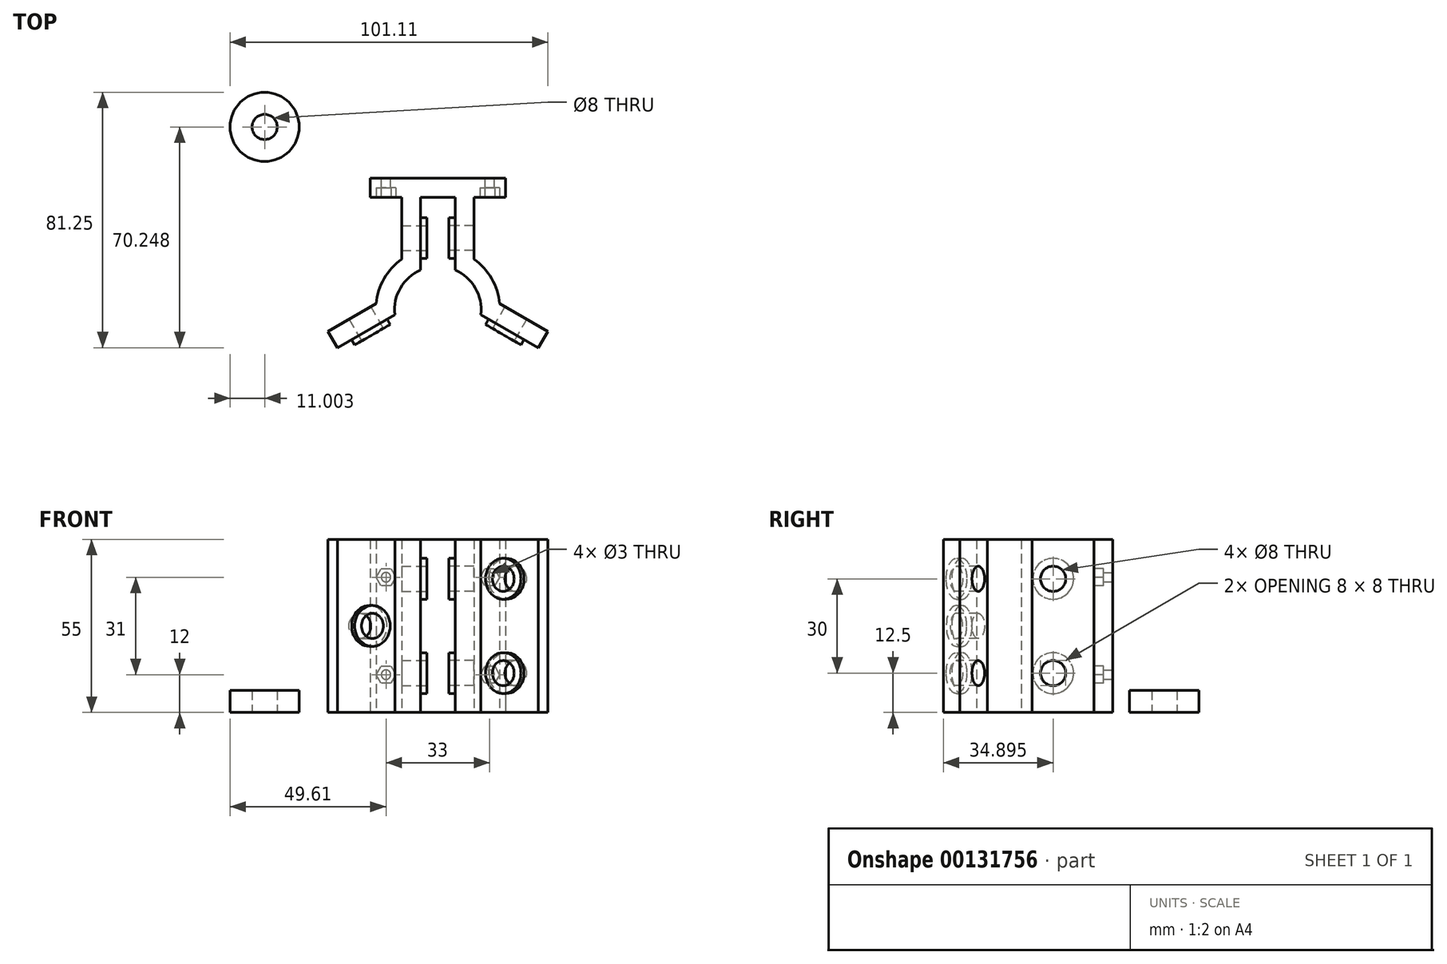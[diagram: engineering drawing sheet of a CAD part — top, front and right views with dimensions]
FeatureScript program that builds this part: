
annotation { "Feature Type Name" : "Feature", "Feature Type Description" : "" }
export const myFeature = defineFeature(function(context is Context, id is Id, definition is map)
    precondition{}
    {
        {
            assignVariable(context, id + "F0", {"name" : "bgap", "anyValue" : 2});
        }
        {
            assignVariable(context, id + "F1", {"name" : "bhole", "anyValue" : 8});
        }
        {
            assignVariable(context, id + "F2", {"name" : "bwidth", "anyValue" : 7});
        }
        {
            assignVariable(context, id + "F3", {"name" : "bdiam", "anyValue" : 22});
        }
        {
            assignVariable(context, id + "F4", {"name" : "width", "anyValue" : 6});
        }
        {
            assignVariable(context, id + "F5", {"name" : "blockLength", "anyValue" : getVariable(context, 'bdiam') * 2 + getVariable(context, 'bdiam') / 2});
        }
        {
            assignVariable(context, id + "F6", {"name" : "mBoltDiam", "anyValue" : 3});
        }
        {
            var Q0;
            Q0=qCreatedBy(makeId("Top.planeOp"),FACE);
            var sketch = newSketch(context, id + "F7", { "sketchPlane" : qUnion([Q0])});
            skCircle(sketch, "E0", {"center": v(0, 0) * mm, "radius": 11.78 * mm, "construction": true});
            skLineSegment(sketch, "E1", {"start": v(0, 0) * mm, "end": v(0, 20) * mm, "construction": true});
            skLineSegment(sketch, "E2", {"start": v(0, 0) * mm, "end": v(-17.32, -10) * mm, "construction": true});
            skLineSegment(sketch, "E3", {"start": v(0, 0) * mm, "end": v(17.32, -10) * mm, "construction": true});
            skPoint(sketch, "E4", {"position": v(0, 22.77) * mm});
            skPoint(sketch, "E5", {"position": v(19.72, -11.39) * mm});
            skPoint(sketch, "E6", {"position": v(-19.72, -11.39) * mm});
            skLineSegment(sketch, "E7.bottom", {"start": v(-3.5, 33.77) * mm, "end": v(3.5, 33.77) * mm, "construction": true});
            skLineSegment(sketch, "E7.top", {"start": v(-3.5, 11.78) * mm, "end": v(3.5, 11.78) * mm, "construction": true});
            skLineSegment(sketch, "E7.left", {"start": v(-3.5, 33.77) * mm, "end": v(-3.5, 11.78) * mm, "construction": true});
            skLineSegment(sketch, "E7.right", {"start": v(3.5, 33.77) * mm, "end": v(3.5, 11.78) * mm, "construction": true});
            skLineSegment(sketch, "E8", {"start": v(-31, -13.86) * mm, "end": v(-27.5, -19.92) * mm, "construction": true});
            skLineSegment(sketch, "E9", {"start": v(-27.5, -19.92) * mm, "end": v(-8.45, -8.92) * mm, "construction": true});
            skLineSegment(sketch, "E10", {"start": v(-8.45, -8.92) * mm, "end": v(-11.95, -2.86) * mm, "construction": true});
            skLineSegment(sketch, "E11", {"start": v(-11.95, -2.86) * mm, "end": v(-31, -13.86) * mm, "construction": true});
            skLineSegment(sketch, "E12", {"start": v(31, -13.86) * mm, "end": v(27.5, -19.92) * mm, "construction": true});
            skLineSegment(sketch, "E13", {"start": v(27.5, -19.92) * mm, "end": v(8.45, -8.92) * mm, "construction": true});
            skLineSegment(sketch, "E14", {"start": v(8.45, -8.92) * mm, "end": v(11.95, -2.86) * mm, "construction": true});
            skLineSegment(sketch, "E15", {"start": v(11.95, -2.86) * mm, "end": v(31, -13.86) * mm, "construction": true});
            skLineSegment(sketch, "E16", {"start": v(-31, -13.86) * mm, "end": v(-36, -5.2) * mm, "construction": true});
            skLineSegment(sketch, "E17", {"start": v(-27.5, -19.92) * mm, "end": v(-22.5, -28.58) * mm, "construction": true});
            skLineSegment(sketch, "E18", {"start": v(27.5, -19.92) * mm, "end": v(22.5, -28.58) * mm, "construction": true});
            skLineSegment(sketch, "E19", {"start": v(31, -13.86) * mm, "end": v(36, -5.2) * mm, "construction": true});
            skSolve(sketch);
        }
        {
            var Q0;
            Q0=qCreatedBy(makeId("Top.planeOp"),FACE);
            var sketch = newSketch(context, id + "F8", { "sketchPlane" : qUnion([Q0])});
            skLineSegment(sketch, "E20", {"start": v(-5.5, 12.63) * mm, "end": v(-5.5, 35.78) * mm});
            skLineSegment(sketch, "E21", {"start": v(-5.5, 35.77) * mm, "end": v(5.5, 35.77) * mm});
            skLineSegment(sketch, "E22", {"start": v(5.5, 35.77) * mm, "end": v(5.5, 12.63) * mm});
            skLineSegment(sketch, "E23", {"start": v(-11.5, 16.09) * mm, "end": v(-11.5, 41.77) * mm});
            skLineSegment(sketch, "E24", {"start": v(-11.5, 41.77) * mm, "end": v(11.5, 41.77) * mm});
            skLineSegment(sketch, "E25", {"start": v(11.5, 41.77) * mm, "end": v(11.5, 16.09) * mm});
            skArc(sketch, "E26", {"start": v(13.69, -1.55) * mm, "mid": v(11.93, 6.89) * mm, "end": v(5.5, 12.63) * mm});
            skArc(sketch, "E27", {"start": v(-13.69, -1.55) * mm, "mid": v(-11.93, 6.89) * mm, "end": v(-5.5, 12.63) * mm});
            skLineSegment(sketch, "E28", {"start": v(-32, -12.12) * mm, "end": v(-35, -6.93) * mm});
            skLineSegment(sketch, "E29", {"start": v(-35, -6.93) * mm, "end": v(-19.68, 1.92) * mm});
            skArc(sketch, "E30", {"start": v(-19.68, 1.92) * mm, "mid": v(-17.13, 9.89) * mm, "end": v(-11.5, 16.09) * mm});
            skLineSegment(sketch, "E31", {"start": v(32, -12.12) * mm, "end": v(35, -6.93) * mm});
            skLineSegment(sketch, "E32", {"start": v(35, -6.93) * mm, "end": v(19.68, 1.92) * mm});
            skArc(sketch, "E33", {"start": v(11.5, 16.09) * mm, "mid": v(17.13, 9.89) * mm, "end": v(19.68, 1.92) * mm});
            skLineSegment(sketch, "E34", {"start": v(-13.69, -1.55) * mm, "end": v(-32, -12.12) * mm});
            skLineSegment(sketch, "E35", {"start": v(13.69, -1.55) * mm, "end": v(32, -12.12) * mm});
            skLineSegment(sketch, "E36", {"start": v(-11.5, 35.78) * mm, "end": v(-21.5, 35.78) * mm});
            skLineSegment(sketch, "E37", {"start": v(-21.5, 35.78) * mm, "end": v(-21.5, 41.77) * mm});
            skLineSegment(sketch, "E38", {"start": v(-21.5, 41.77) * mm, "end": v(-11.5, 41.77) * mm});
            skLineSegment(sketch, "E39", {"start": v(11.5, 35.77) * mm, "end": v(21.5, 35.77) * mm});
            skLineSegment(sketch, "E40", {"start": v(21.5, 35.77) * mm, "end": v(21.5, 41.77) * mm});
            skLineSegment(sketch, "E41", {"start": v(21.5, 41.77) * mm, "end": v(11.5, 41.77) * mm});
            skSolve(sketch);
        }
        {
            var Q0;
            {var subQ4=sQuery(id+"F8.wireOp",EDGE,"H4ZlZzYq-pDdm-UTQ2-Dq43-ZovsfROqYDKv");Q0=makeQuery(id+"F8.imprint","IMPRINT",FACE,{"disambiguationData":[TD([[makeQuery(id+"F8.imprint","IMPRINT",EDGE,{"derivedFrom":subQ4}),-1.0]])]});}
            var Q1;
            {var subQ1=sQuery(id+"F8.wireOp",EDGE,"BFLWIUzv-WRI4-VLCz-G4py-bszHORUKPSnW");var subQ5=sQuery(id+"F8.wireOp",EDGE,"E20");var subQ6=makeQuery(id+"F8.imprint","INTERSECT",VERTEX,{"derivedFrom":[subQ1,subQ5]});Q1=makeQuery(id+"F8.imprint","IMPRINT",FACE,{"disambiguationData":[TD([[makeQuery(id+"F8.imprint","IMPRINT",EDGE,{"disambiguationData":[TD([[subQ6,-1.0]])],"derivedFrom":subQ1}),-1.0]])]});}
            var Q2;
            {var subQ0=sQuery(id+"F8.wireOp",EDGE,"E21");Q2=makeQuery(id+"F8.imprint","IMPRINT",FACE,{"disambiguationData":[TD([[makeQuery(id+"F8.imprint","IMPRINT",EDGE,{"derivedFrom":subQ0}),1.0]])]});}
            var Q3;
            {var subQ1=sQuery(id+"F8.wireOp",EDGE,"BFLWIUzv-WRI4-VLCz-G4py-bszHORUKPSnW");var subQ7=sQuery(id+"F8.wireOp",EDGE,"E22");var subQ8=makeQuery(id+"F8.imprint","INTERSECT",VERTEX,{"derivedFrom":[subQ1,subQ7]});Q3=makeQuery(id+"F8.imprint","IMPRINT",FACE,{"disambiguationData":[TD([[makeQuery(id+"F8.imprint","IMPRINT",EDGE,{"disambiguationData":[TD([[subQ8,1.0]])],"derivedFrom":subQ1}),-1.0]])]});}
            var Q4;
            {var subQ4=sQuery(id+"F8.wireOp",EDGE,"XH5RXwVZ-MuUo-YG4h-DYCp-uCzL1HIl9ywU");Q4=makeQuery(id+"F8.imprint","IMPRINT",FACE,{"disambiguationData":[TD([[makeQuery(id+"F8.imprint","IMPRINT",EDGE,{"derivedFrom":subQ4}),-1.0]])]});}
            var Q5;
            {var subQ0=sQuery(id+"F8.wireOp",EDGE,"uJ7mwRlV-UdIp-EGwW-voM6-Ei8UeiCH7yjD");Q5=makeQuery(id+"F8.imprint","IMPRINT",FACE,{"disambiguationData":[TD([[makeQuery(id+"F8.imprint","IMPRINT",EDGE,{"derivedFrom":subQ0}),-1.0]])]});}
            var Q6;
            {var subQ0=sQuery(id+"F8.wireOp",EDGE,"ePywylGH-YD8d-p93b-p2H9-ijm7IqbQ1sYN");Q6=makeQuery(id+"F8.imprint","IMPRINT",FACE,{"disambiguationData":[TD([[makeQuery(id+"F8.imprint","IMPRINT",EDGE,{"derivedFrom":subQ0}),1.0]])]});}
            var Q7;
            {var subQ2=sQuery(id+"F8.wireOp",EDGE,"E36");Q7=makeQuery(id+"F8.imprint","IMPRINT",FACE,{"disambiguationData":[TD([[makeQuery(id+"F8.imprint","IMPRINT",EDGE,{"derivedFrom":subQ2}),-1.0]])]});}
            var Q8;
            {var subQ2=sQuery(id+"F8.wireOp",EDGE,"E39");Q8=makeQuery(id+"F8.imprint","IMPRINT",FACE,{"disambiguationData":[TD([[makeQuery(id+"F8.imprint","IMPRINT",EDGE,{"derivedFrom":subQ2}),1.0]])]});}
            extrude(context, id + "F9", {"entities" : qUnion([Q0, Q1, Q2, Q3, Q4, Q5, Q6, Q7, Q8]), "depth" : (getVariable(context, 'blockLength')) * mm});
        }
        {
            var Q0;
            Q0=qCreatedBy(makeId("Top.planeOp"),FACE);
            var sketch = newSketch(context, id + "F10", { "sketchPlane" : qUnion([Q0])});
            skCircle(sketch, "E42", {"center": v(-55.1, 58.13) * mm, "radius": 11 * mm});
            skCircle(sketch, "E43", {"center": v(-55.1, 58.13) * mm, "radius": 4 * mm});
            skSolve(sketch);
        }
        {
            var Q0;
            Q0=makeQuery(id+"F10.imprint","IMPRINT",FACE,{"disambiguationData":[TD([[makeQuery(id+"F10.imprint","IMPRINT",EDGE,{"derivedFrom":sQuery(id+"F10.wireOp",EDGE,"E42")}),1.0]])]});
            extrude(context, id + "F11", {"entities" : qUnion([Q0]), "depth" : (getVariable(context, 'bwidth')) * mm});
        }
        {
            var Q0;
            Q0=makeQuery(id+"F9.opExtrude","SWEPT_FACE",FACE,{"disambiguationData":[OSD([sQuery(id+"F8.wireOp",EDGE,"E34")])]});
            var sketch = newSketch(context, id + "F12", { "sketchPlane" : qUnion([Q0])});
            skPoint(sketch, "E44", {"position": v(-22, 27.5) * mm});
            skPoint(sketch, "E44.positionSnap0", {"position": v(-33.78, 27.5) * mm});
            skCircle(sketch, "E45", {"center": v(-22, 27.5) * mm, "radius": 6.5 * mm});
            skSolve(sketch);
        }
        {
            var Q0;
            Q0=makeQuery(id+"F9.opExtrude","SWEPT_FACE",FACE,{"disambiguationData":[OSD([sQuery(id+"F8.wireOp",EDGE,"E35")])]});
            var sketch = newSketch(context, id + "F13", { "sketchPlane" : qUnion([Q0])});
            skPoint(sketch, "E46", {"position": v(33.77, 42.5) * mm});
            skPoint(sketch, "E47", {"position": v(33.77, 12.5) * mm});
            skPoint(sketch, "E48", {"position": v(33.77, 27.5) * mm});
            skPoint(sketch, "E49", {"position": v(22, 42.5) * mm});
            skPoint(sketch, "E50", {"position": v(22, 12.5) * mm});
            skCircle(sketch, "E51", {"center": v(22, 42.5) * mm, "radius": 6.5 * mm});
            skCircle(sketch, "E52", {"center": v(22, 12.5) * mm, "radius": 6.5 * mm});
            skSolve(sketch);
        }
        {
            var Q0;
            Q0=makeQuery(id+"F9.opExtrude","SWEPT_FACE",FACE,{"disambiguationData":[OSD([sQuery(id+"F8.wireOp",EDGE,"E22")])]});
            var sketch = newSketch(context, id + "F14", { "sketchPlane" : qUnion([Q0])});
            skPoint(sketch, "E53", {"position": v(-22.77, 0) * mm});
            skPoint(sketch, "E54", {"position": v(-12.63, 27.5) * mm});
            skPoint(sketch, "E55", {"position": v(-22.78, 12.5) * mm});
            skPoint(sketch, "E56", {"position": v(-22.78, 42.5) * mm});
            skCircle(sketch, "E57", {"center": v(-22.78, 12.5) * mm, "radius": 6.5 * mm});
            skCircle(sketch, "E58", {"center": v(-22.78, 42.5) * mm, "radius": 6.5 * mm});
            skSolve(sketch);
        }
        {
            var Q0;
            Q0=makeQuery(id+"F9.opExtrude","SWEPT_FACE",FACE,{"disambiguationData":[OSD([sQuery(id+"F8.wireOp",EDGE,"E20")])]});
            var sketch = newSketch(context, id + "F15", { "sketchPlane" : qUnion([Q0])});
            skPoint(sketch, "E59", {"position": v(22.77, 0) * mm});
            skCircle(sketch, "E60", {"center": v(22.77, 12.5) * mm, "radius": 6.5 * mm});
            skCircle(sketch, "E61", {"center": v(22.77, 42.5) * mm, "radius": 6.5 * mm});
            skPoint(sketch, "E62", {"position": v(12.63, 27.5) * mm});
            skSolve(sketch);
        }
        {
            var Q0;
            Q0=makeQuery(id+"F12.imprint","IMPRINT",FACE,{"disambiguationData":[TD([[makeQuery(id+"F12.imprint","IMPRINT",EDGE,{"derivedFrom":sQuery(id+"F12.wireOp",EDGE,"E45")}),1.0]])]});
            extrude(context, id + "F16", {"entities" : qUnion([Q0]), "operationType" : NewBodyOperationType.ADD, "depth" : (getVariable(context, 'bgap')) * mm});
        }
        {
            var Q0;
            Q0=sQuery(id+"F13.wireOp",VERTEX,"E49");
            var Q1;
            Q1=sQuery(id+"F13.wireOp",VERTEX,"E50");
            var Q2;
            Q2=sQuery(id+"F12.wireOp",VERTEX,"E44");
            var Q3;
            Q3=sQuery(id+"F14.wireOp",VERTEX,"E56");
            var Q4;
            Q4=sQuery(id+"F15.wireOp",VERTEX,"E61.center");
            var Q5;
            Q5=sQuery(id+"F15.wireOp",VERTEX,"E60.center");
            var Q6;
            Q6=sQuery(id+"F14.wireOp",VERTEX,"E55");
            var Q7;
            Q7=makeQuery(id+"F9.opExtrude","SWEPT_BODY",BODY,{"disambiguationData":[OSD([sQuery(id+"F8.wireOp",EDGE,"E20"),sQuery(id+"F8.wireOp",EDGE,"E21"),sQuery(id+"F8.wireOp",EDGE,"E22"),sQuery(id+"F8.wireOp",EDGE,"E23"),sQuery(id+"F8.wireOp",EDGE,"E24"),sQuery(id+"F8.wireOp",EDGE,"E25"),sQuery(id+"F8.wireOp",EDGE,"E26"),sQuery(id+"F8.wireOp",EDGE,"E27"),sQuery(id+"F8.wireOp",EDGE,"E28"),sQuery(id+"F8.wireOp",EDGE,"E29"),sQuery(id+"F8.wireOp",EDGE,"E30"),sQuery(id+"F8.wireOp",EDGE,"E31"),sQuery(id+"F8.wireOp",EDGE,"E32"),sQuery(id+"F8.wireOp",EDGE,"E33"),sQuery(id+"F8.wireOp",EDGE,"E34"),sQuery(id+"F8.wireOp",EDGE,"E35")])]});
            hole(context, id + "F17", {"style" : HoleStyle.SIMPLE, "endStyle" : HoleEndStyle.THROUGH, "holeDiameter" : (getVariable(context, 'bhole')) * mm, "startFromSketch" : true, "locations" : qUnion([Q0, Q1, Q2, Q3, Q4, Q5, Q6]), "scope" : qUnion([Q7]), "isTappedThrough" : true});
        }
        {
            var Q0;
            Q0=makeQuery(id+"F13.imprint","IMPRINT",FACE,{"disambiguationData":[TD([[makeQuery(id+"F13.imprint","IMPRINT",EDGE,{"derivedFrom":sQuery(id+"F13.wireOp",EDGE,"E52")}),1.0]])]});
            var Q1;
            Q1=makeQuery(id+"F13.imprint","IMPRINT",FACE,{"disambiguationData":[TD([[makeQuery(id+"F13.imprint","IMPRINT",EDGE,{"derivedFrom":sQuery(id+"F13.wireOp",EDGE,"E51")}),1.0]])]});
            extrude(context, id + "F18", {"entities" : qUnion([Q0, Q1]), "operationType" : NewBodyOperationType.ADD, "depth" : (getVariable(context, 'bgap')) * mm});
        }
        {
            var Q0;
            Q0=makeQuery(id+"F15.imprint","IMPRINT",FACE,{"disambiguationData":[TD([[makeQuery(id+"F15.imprint","IMPRINT",EDGE,{"derivedFrom":sQuery(id+"F15.wireOp",EDGE,"E60")}),1.0]])]});
            var Q1;
            Q1=makeQuery(id+"F15.imprint","IMPRINT",FACE,{"disambiguationData":[TD([[makeQuery(id+"F15.imprint","IMPRINT",EDGE,{"derivedFrom":sQuery(id+"F15.wireOp",EDGE,"E61")}),1.0]])]});
            extrude(context, id + "F19", {"entities" : qUnion([Q0, Q1]), "operationType" : NewBodyOperationType.ADD, "depth" : (getVariable(context, 'bgap')) * mm});
        }
        {
            var Q0;
            Q0=makeQuery(id+"F14.imprint","IMPRINT",FACE,{"disambiguationData":[TD([[makeQuery(id+"F14.imprint","IMPRINT",EDGE,{"derivedFrom":sQuery(id+"F14.wireOp",EDGE,"E57")}),1.0]])]});
            var Q1;
            Q1=makeQuery(id+"F14.imprint","IMPRINT",FACE,{"disambiguationData":[TD([[makeQuery(id+"F14.imprint","IMPRINT",EDGE,{"derivedFrom":sQuery(id+"F14.wireOp",EDGE,"E58")}),1.0]])]});
            extrude(context, id + "F20", {"entities" : qUnion([Q0, Q1]), "operationType" : NewBodyOperationType.ADD, "depth" : (getVariable(context, 'bgap')) * mm});
        }
        {
            var Q0;
            Q0=sQuery(id+"F12.wireOp",VERTEX,"E44");
            var Q1;
            Q1=sQuery(id+"F15.wireOp",VERTEX,"E61.center");
            var Q2;
            Q2=sQuery(id+"F15.wireOp",VERTEX,"E60.center");
            var Q3;
            Q3=sQuery(id+"F13.wireOp",VERTEX,"E49");
            var Q4;
            Q4=sQuery(id+"F13.wireOp",VERTEX,"E50");
            var Q5;
            Q5=makeQuery(id+"F9.opExtrude","SWEPT_BODY",BODY,{"disambiguationData":[OSD([sQuery(id+"F8.wireOp",EDGE,"E20"),sQuery(id+"F8.wireOp",EDGE,"E21"),sQuery(id+"F8.wireOp",EDGE,"E22"),sQuery(id+"F8.wireOp",EDGE,"E23"),sQuery(id+"F8.wireOp",EDGE,"E24"),sQuery(id+"F8.wireOp",EDGE,"E25"),sQuery(id+"F8.wireOp",EDGE,"E26"),sQuery(id+"F8.wireOp",EDGE,"E27"),sQuery(id+"F8.wireOp",EDGE,"E28"),sQuery(id+"F8.wireOp",EDGE,"E29"),sQuery(id+"F8.wireOp",EDGE,"E30"),sQuery(id+"F8.wireOp",EDGE,"E31"),sQuery(id+"F8.wireOp",EDGE,"E32"),sQuery(id+"F8.wireOp",EDGE,"E33"),sQuery(id+"F8.wireOp",EDGE,"E34"),sQuery(id+"F8.wireOp",EDGE,"E35")])]});
            hole(context, id + "F21", {"style" : HoleStyle.SIMPLE, "endStyle" : HoleEndStyle.THROUGH, "oppositeDirection" : true, "holeDiameter" : (getVariable(context, 'bhole')) * mm, "startFromSketch" : true, "locations" : qUnion([Q0, Q1, Q2, Q3, Q4]), "scope" : qUnion([Q5]), "isTappedThrough" : true});
        }
        {
            var Q0;
            Q0=makeQuery(id+"F9.opExtrude","SWEPT_FACE",FACE,{"disambiguationData":[OSD([sQuery(id+"F8.wireOp",EDGE,"E24"),sQuery(id+"F8.wireOp",EDGE,"E38"),sQuery(id+"F8.wireOp",EDGE,"E41")])]});
            var sketch = newSketch(context, id + "F22", { "sketchPlane" : qUnion([Q0])});
            skPoint(sketch, "E63", {"position": v(-16.5, 43) * mm});
            skPoint(sketch, "E64", {"position": v(16.5, 43) * mm});
            skPoint(sketch, "E65", {"position": v(16.5, 12) * mm});
            skPoint(sketch, "E66", {"position": v(-16.5, 12) * mm});
            skLineSegment(sketch, "E67.bottom", {"start": v(-16.5, 43) * mm, "end": v(16.5, 43) * mm});
            skLineSegment(sketch, "E67.top", {"start": v(-16.5, 12) * mm, "end": v(16.5, 12) * mm});
            skLineSegment(sketch, "E67.left", {"start": v(-16.5, 43) * mm, "end": v(-16.5, 12) * mm});
            skLineSegment(sketch, "E67.right", {"start": v(16.5, 43) * mm, "end": v(16.5, 12) * mm});
            skSolve(sketch);
        }
        {
            var Q0;
            Q0=sQuery(id+"F22.wireOp",VERTEX,"E65");
            var Q1;
            Q1=sQuery(id+"F22.wireOp",VERTEX,"E66");
            var Q2;
            Q2=sQuery(id+"F22.wireOp",VERTEX,"E63");
            var Q3;
            Q3=sQuery(id+"F22.wireOp",VERTEX,"E64");
            var Q4;
            Q4=makeQuery(id+"F9.opExtrude","SWEPT_BODY",BODY,{"disambiguationData":[OSD([sQuery(id+"F8.wireOp",EDGE,"E20"),sQuery(id+"F8.wireOp",EDGE,"E21"),sQuery(id+"F8.wireOp",EDGE,"E22"),sQuery(id+"F8.wireOp",EDGE,"E23"),sQuery(id+"F8.wireOp",EDGE,"E24"),sQuery(id+"F8.wireOp",EDGE,"E25"),sQuery(id+"F8.wireOp",EDGE,"E26"),sQuery(id+"F8.wireOp",EDGE,"E27"),sQuery(id+"F8.wireOp",EDGE,"E28"),sQuery(id+"F8.wireOp",EDGE,"E29"),sQuery(id+"F8.wireOp",EDGE,"E30"),sQuery(id+"F8.wireOp",EDGE,"E31"),sQuery(id+"F8.wireOp",EDGE,"E32"),sQuery(id+"F8.wireOp",EDGE,"E33"),sQuery(id+"F8.wireOp",EDGE,"E34"),sQuery(id+"F8.wireOp",EDGE,"E35"),sQuery(id+"F8.wireOp",EDGE,"E36"),sQuery(id+"F8.wireOp",EDGE,"E37"),sQuery(id+"F8.wireOp",EDGE,"E38"),sQuery(id+"F8.wireOp",EDGE,"E39"),sQuery(id+"F8.wireOp",EDGE,"E40"),sQuery(id+"F8.wireOp",EDGE,"E41")])]});
            hole(context, id + "F23", {"style" : HoleStyle.SIMPLE, "endStyle" : HoleEndStyle.BLIND, "holeDiameter" : (getVariable(context, 'mBoltDiam')) * mm, "holeDepth" : (getVariable(context, 'width')) * mm, "startFromSketch" : true, "locations" : qUnion([Q0, Q1, Q2, Q3]), "scope" : qUnion([Q4])});
        }
        {
            var Q0;
            Q0=makeQuery(id+"F9.opExtrude","SWEPT_FACE",FACE,{"disambiguationData":[OSD([sQuery(id+"F8.wireOp",EDGE,"E39")])]});
            var sketch = newSketch(context, id + "F24", { "sketchPlane" : qUnion([Q0])});
            skCircle(sketch, "E68.cCircle", {"center": v(16.5, 43) * mm, "radius": 2.7 * mm, "construction": true});
            skLineSegment(sketch, "E68.0", {"start": v(14.94, 45.7) * mm, "end": v(18.06, 45.7) * mm});
            skLineSegment(sketch, "E68.1", {"start": v(18.06, 45.7) * mm, "end": v(19.62, 43) * mm});
            skLineSegment(sketch, "E68.2", {"start": v(19.62, 43) * mm, "end": v(18.06, 40.3) * mm});
            skLineSegment(sketch, "E68.3", {"start": v(18.06, 40.3) * mm, "end": v(14.94, 40.3) * mm});
            skLineSegment(sketch, "E68.4", {"start": v(14.94, 40.3) * mm, "end": v(13.38, 43) * mm});
            skLineSegment(sketch, "E68.5", {"start": v(13.38, 43) * mm, "end": v(14.94, 45.7) * mm});
            skPoint(sketch, "E68.0.midPoint", {"position": v(16.5, 45.7) * mm});
            skCircle(sketch, "E69.cCircle", {"center": v(16.5, 12) * mm, "radius": 2.7 * mm, "construction": true});
            skLineSegment(sketch, "E69.0", {"start": v(14.94, 14.7) * mm, "end": v(18.06, 14.7) * mm});
            skLineSegment(sketch, "E69.1", {"start": v(18.06, 14.7) * mm, "end": v(19.62, 12) * mm});
            skLineSegment(sketch, "E69.2", {"start": v(19.62, 12) * mm, "end": v(18.06, 9.3) * mm});
            skLineSegment(sketch, "E69.3", {"start": v(18.06, 9.3) * mm, "end": v(14.94, 9.3) * mm});
            skLineSegment(sketch, "E69.4", {"start": v(14.94, 9.3) * mm, "end": v(13.38, 12) * mm});
            skLineSegment(sketch, "E69.5", {"start": v(13.38, 12) * mm, "end": v(14.94, 14.7) * mm});
            skPoint(sketch, "E69.0.midPoint", {"position": v(16.5, 14.7) * mm});
            skCircle(sketch, "E70.cCircle", {"center": v(-16.5, 43) * mm, "radius": 2.7 * mm, "construction": true});
            skLineSegment(sketch, "E70.0", {"start": v(-18.06, 45.7) * mm, "end": v(-14.94, 45.7) * mm});
            skLineSegment(sketch, "E70.1", {"start": v(-14.94, 45.7) * mm, "end": v(-13.38, 43) * mm});
            skLineSegment(sketch, "E70.2", {"start": v(-13.38, 43) * mm, "end": v(-14.94, 40.3) * mm});
            skLineSegment(sketch, "E70.3", {"start": v(-14.94, 40.3) * mm, "end": v(-18.06, 40.3) * mm});
            skLineSegment(sketch, "E70.4", {"start": v(-18.06, 40.3) * mm, "end": v(-19.62, 43) * mm});
            skLineSegment(sketch, "E70.5", {"start": v(-19.62, 43) * mm, "end": v(-18.06, 45.7) * mm});
            skPoint(sketch, "E70.0.midPoint", {"position": v(-16.5, 45.7) * mm});
            skCircle(sketch, "E71.cCircle", {"center": v(-16.5, 12) * mm, "radius": 2.7 * mm, "construction": true});
            skLineSegment(sketch, "E71.0", {"start": v(-14.94, 9.3) * mm, "end": v(-18.06, 9.3) * mm});
            skLineSegment(sketch, "E71.1", {"start": v(-18.06, 9.3) * mm, "end": v(-19.62, 12) * mm});
            skLineSegment(sketch, "E71.2", {"start": v(-19.62, 12) * mm, "end": v(-18.06, 14.7) * mm});
            skLineSegment(sketch, "E71.3", {"start": v(-18.06, 14.7) * mm, "end": v(-14.94, 14.7) * mm});
            skLineSegment(sketch, "E71.4", {"start": v(-14.94, 14.7) * mm, "end": v(-13.38, 12) * mm});
            skLineSegment(sketch, "E71.5", {"start": v(-13.38, 12) * mm, "end": v(-14.94, 9.3) * mm});
            skPoint(sketch, "E71.0.midPoint", {"position": v(-16.5, 9.3) * mm});
            skSolve(sketch);
        }
        {
            var Q0;
            Q0=makeQuery(id+"F24.imprint","IMPRINT",FACE,{"disambiguationData":[TD([[makeQuery(id+"F24.imprint","IMPRINT",EDGE,{"derivedFrom":sQuery(id+"F24.wireOp",EDGE,"E71.0")}),-1.0]])]});
            var Q1;
            Q1=makeQuery(id+"F24.imprint","IMPRINT",FACE,{"disambiguationData":[TD([[makeQuery(id+"F24.imprint","IMPRINT",EDGE,{"derivedFrom":sQuery(id+"F24.wireOp",EDGE,"E70.0")}),-1.0]])]});
            var Q2;
            Q2=makeQuery(id+"F24.imprint","IMPRINT",FACE,{"disambiguationData":[TD([[makeQuery(id+"F24.imprint","IMPRINT",EDGE,{"derivedFrom":sQuery(id+"F24.wireOp",EDGE,"E69.0")}),-1.0]])]});
            var Q3;
            Q3=makeQuery(id+"F24.imprint","IMPRINT",FACE,{"disambiguationData":[TD([[makeQuery(id+"F24.imprint","IMPRINT",EDGE,{"derivedFrom":sQuery(id+"F24.wireOp",EDGE,"E68.0")}),-1.0]])]});
            extrude(context, id + "F25", {"entities" : qUnion([Q0, Q1, Q2, Q3]), "operationType" : NewBodyOperationType.REMOVE, "oppositeDirection" : true, "depth" : 3 * mm});
        }
    });
